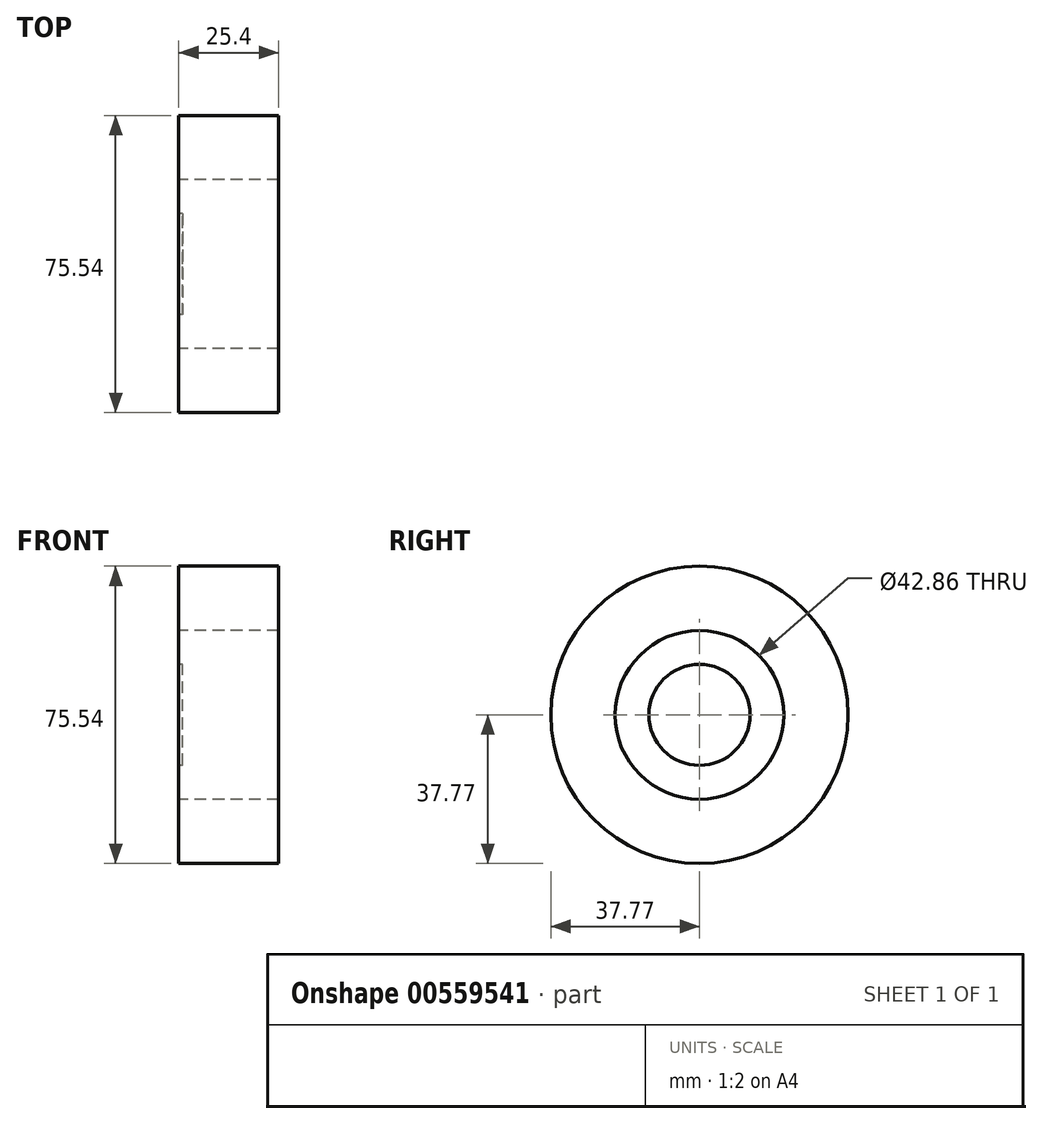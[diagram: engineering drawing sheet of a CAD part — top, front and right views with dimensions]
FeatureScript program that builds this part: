
annotation { "Feature Type Name" : "Feature", "Feature Type Description" : "" }
export const myFeature = defineFeature(function(context is Context, id is Id, definition is map)
    precondition{}
    {
        {
            var Q0;
            Q0=qCreatedBy(makeId("Right.planeOp"),FACE);
            var sketch = newSketch(context, id + "F0", { "sketchPlane" : qUnion([Q0])});
            skCircle(sketch, "E0", {"center": v(0, 0) * mm, "radius": 37.77 * mm});
            skCircle(sketch, "E1", {"center": v(0, 0) * mm, "radius": 21.43 * mm});
            skCircle(sketch, "E2", {"center": v(0, 0) * mm, "radius": 12.84 * mm});
            skSolve(sketch);
        }
        {
            var Q0;
            Q0=makeQuery(id+"F0.imprint","IMPRINT",FACE,{"disambiguationData":[TD([[makeQuery(id+"F0.imprint","IMPRINT",EDGE,{"derivedFrom":sQuery(id+"F0.wireOp",EDGE,"E0")}),1.0]])]});
            var Q1;
            Q1=makeQuery(id+"F0.imprint","IMPRINT",FACE,{"disambiguationData":[TD([[makeQuery(id+"F0.imprint","IMPRINT",EDGE,{"derivedFrom":sQuery(id+"F0.wireOp",EDGE,"E2")}),1.0]])]});
            extrude(context, id + "F1", {"entities" : qUnion([Q0, Q1]), "depth" : mm, "offsetDistance" : 25.4 * mm});
        }
        {
            var Q0;
            Q0 = qSketchRegion(id + "F0", true);
            extrude(context, id + "F2", {"entities" : qUnion([Q0]), "operationType" : NewBodyOperationType.ADD, "depth" : 25.4 * mm, "offsetDistance" : 25.4 * mm});
        }
    });
